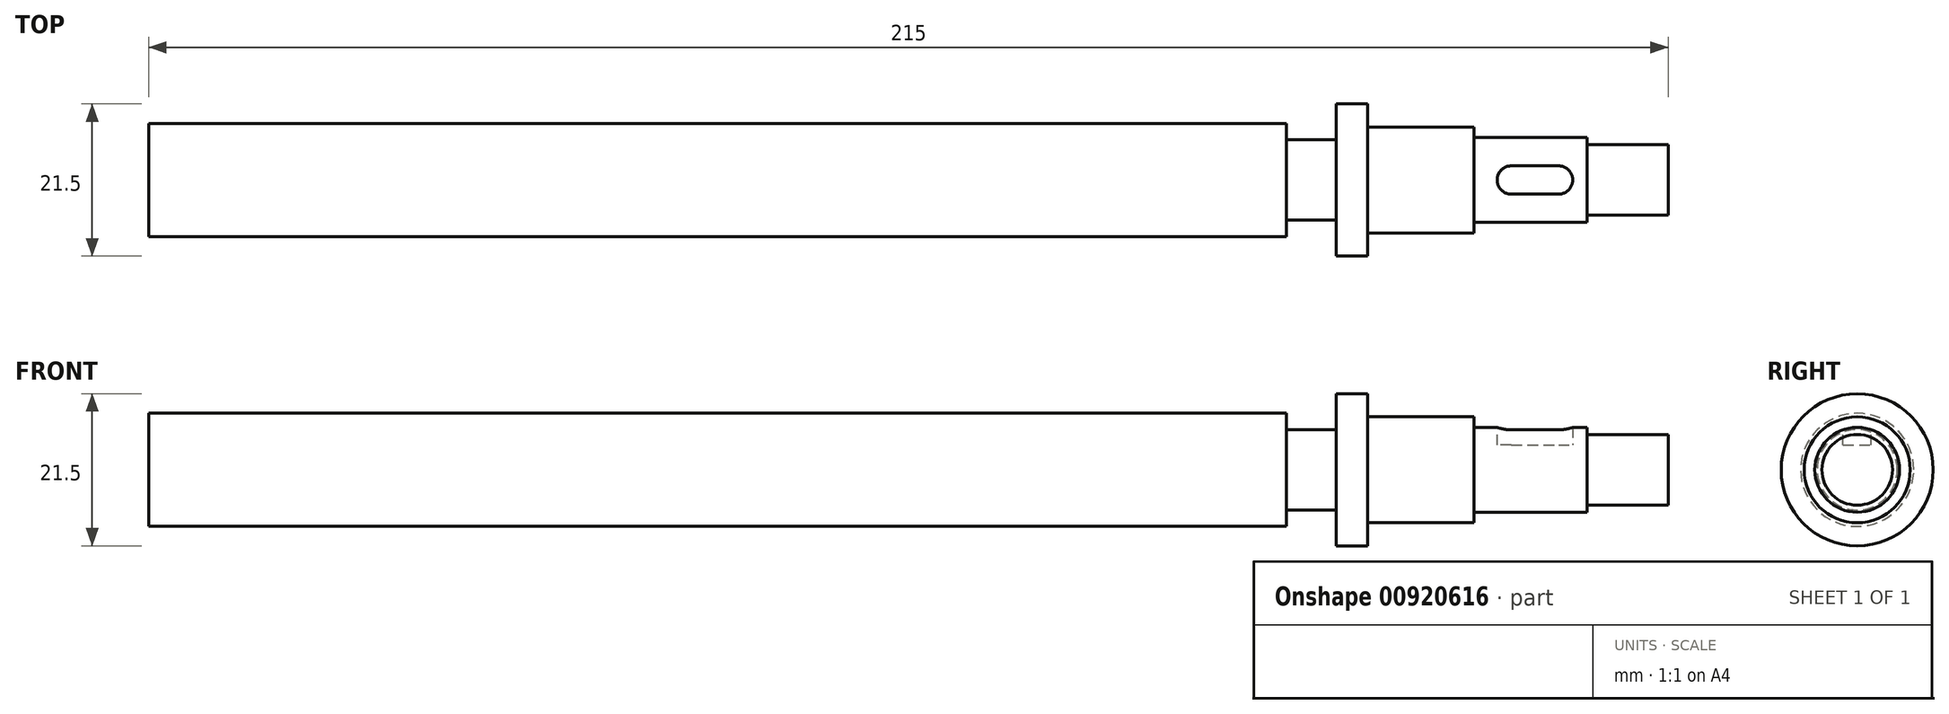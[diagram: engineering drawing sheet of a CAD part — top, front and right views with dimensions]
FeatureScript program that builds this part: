
annotation { "Feature Type Name" : "Feature", "Feature Type Description" : "" }
export const myFeature = defineFeature(function(context is Context, id is Id, definition is map)
    precondition{}
    {
        {
            var Q0;
            Q0=qCreatedBy(makeId("Front.planeOp"),FACE);
            var sketch = newSketch(context, id + "F0", { "sketchPlane" : qUnion([Q0])});
            skLineSegment(sketch, "E0", {"start": v(0, 0) * mm, "end": v(-60.23, 0) * mm, "construction": true});
            skLineSegment(sketch, "E1", {"start": v(0, 0) * mm, "end": v(0, 8) * mm});
            skLineSegment(sketch, "E2", {"start": v(0, 8) * mm, "end": v(161, 8) * mm});
            skLineSegment(sketch, "E3", {"start": v(161, 8) * mm, "end": v(161, 5.68) * mm});
            skLineSegment(sketch, "E4", {"start": v(161, 5.68) * mm, "end": v(168, 5.68) * mm});
            skLineSegment(sketch, "E5", {"start": v(168, 5.68) * mm, "end": v(168, 10.75) * mm});
            skLineSegment(sketch, "E6", {"start": v(168, 10.75) * mm, "end": v(172.5, 10.75) * mm});
            skLineSegment(sketch, "E7", {"start": v(172.5, 10.75) * mm, "end": v(172.5, 7.5) * mm});
            skLineSegment(sketch, "E8", {"start": v(172.5, 7.5) * mm, "end": v(187.5, 7.5) * mm});
            skLineSegment(sketch, "E9", {"start": v(187.5, 7.5) * mm, "end": v(187.5, 6) * mm});
            skLineSegment(sketch, "E10", {"start": v(187.5, 6) * mm, "end": v(203.5, 6) * mm});
            skLineSegment(sketch, "E11", {"start": v(203.5, 6) * mm, "end": v(203.5, 5) * mm});
            skLineSegment(sketch, "E12", {"start": v(203.5, 5) * mm, "end": v(215, 5) * mm});
            skLineSegment(sketch, "E13", {"start": v(215, 5) * mm, "end": v(215, 0) * mm});
            skLineSegment(sketch, "E14", {"start": v(0, 0) * mm, "end": v(215, 0) * mm});
            skSolve(sketch);
        }
        {
            var Q0;
            Q0=makeQuery(id+"F0.imprint","IMPRINT",FACE,{"disambiguationData":[TD([[makeQuery(id+"F0.imprint","IMPRINT",EDGE,{"derivedFrom":sQuery(id+"F0.wireOp",EDGE,"E1")}),-1.0]])]});
            var Q1;
            Q1=sQuery(id+"F0.wireOp",EDGE,"E0");
            revolve(context, id + "F1", {"surfaceOperationType" : NewSurfaceOperationType.NEW, "entities" : qUnion([Q0]), "axis" : qUnion([Q1]), "revolveType" : RevolveType.FULL});
        }
        {
            var Q0;
            Q0=qCreatedBy(makeId("Top.planeOp"),FACE);
            cPlane(context, id + "F2", {"entities" : qUnion([Q0]), "cplaneType" : CPlaneType.OFFSET, "offset" : 7.5 * mm, "width" : 150 * mm, "height" : 150 * mm});
        }
        {
            var Q0;
            Q0=qCreatedBy(id+"F2.planeOp",FACE);
            var sketch = newSketch(context, id + "F3", { "sketchPlane" : qUnion([Q0])});
            skLineSegment(sketch, "E15.bottom", {"start": v(190.8, 2) * mm, "end": v(201.5, 2) * mm});
            skLineSegment(sketch, "E15.top", {"start": v(190.8, -2) * mm, "end": v(201.5, -2) * mm});
            skLineSegment(sketch, "E15.left", {"start": v(190.8, 2) * mm, "end": v(190.8, -2) * mm});
            skLineSegment(sketch, "E15.right", {"start": v(201.5, 2) * mm, "end": v(201.5, -2) * mm});
            skSolve(sketch);
        }
        {
            var Q0;
            Q0=makeQuery(id+"F3.imprint","IMPRINT",FACE,{"disambiguationData":[TD([[makeQuery(id+"F3.imprint","IMPRINT",EDGE,{"derivedFrom":sQuery(id+"F3.wireOp",EDGE,"E15.bottom")}),-1.0]])]});
            extrude(context, id + "F4", {"entities" : qUnion([Q0]), "operationType" : NewBodyOperationType.REMOVE, "oppositeDirection" : true, "depth" : 4 * mm, "offsetDistance" : 25 * mm});
        }
        {
            var Q0;
            Q0=makeQuery(id+"F4.boolean.opBoolean","COPY",EDGE,{"derivedFrom":makeQuery(id+"F4.opExtrude","SWEPT_EDGE",EDGE,{"disambiguationData":[OSD([sQuery(id+"F3.wireOp",EDGE,"E15.bottom"),sQuery(id+"F3.wireOp",EDGE,"E15.left")])]})});
            var Q1;
            Q1=makeQuery(id+"F4.boolean.opBoolean","COPY",EDGE,{"derivedFrom":makeQuery(id+"F4.opExtrude","SWEPT_EDGE",EDGE,{"disambiguationData":[OSD([sQuery(id+"F3.wireOp",EDGE,"E15.bottom"),sQuery(id+"F3.wireOp",EDGE,"E15.right")])]})});
            var Q2;
            Q2=makeQuery(id+"F4.boolean.opBoolean","COPY",EDGE,{"derivedFrom":makeQuery(id+"F4.opExtrude","SWEPT_EDGE",EDGE,{"disambiguationData":[OSD([sQuery(id+"F3.wireOp",EDGE,"E15.top"),sQuery(id+"F3.wireOp",EDGE,"E15.right")])]})});
            var Q3;
            Q3=makeQuery(id+"F4.boolean.opBoolean","COPY",EDGE,{"derivedFrom":makeQuery(id+"F4.opExtrude","SWEPT_EDGE",EDGE,{"disambiguationData":[OSD([sQuery(id+"F3.wireOp",EDGE,"E15.top"),sQuery(id+"F3.wireOp",EDGE,"E15.left")])]})});
            fillet(context, id + "F5", {"entities" : qUnion([Q0, Q1, Q2, Q3]), "radius" : 2 * mm, "tangentPropagation" : true, "allowEdgeOverflow" : false});
        }
    });
